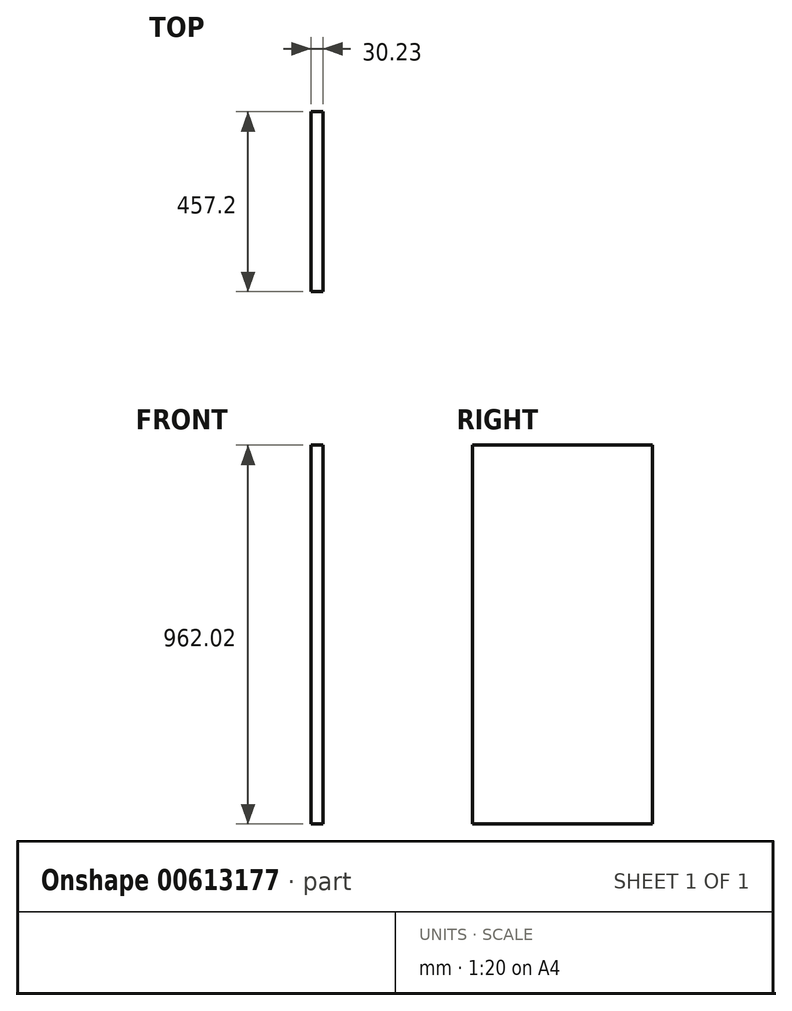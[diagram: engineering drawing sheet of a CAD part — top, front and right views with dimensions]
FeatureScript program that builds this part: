
annotation { "Feature Type Name" : "Feature", "Feature Type Description" : "" }
export const myFeature = defineFeature(function(context is Context, id is Id, definition is map)
    precondition{}
    {
        {
            var Q0;
            Q0=qCreatedBy(makeId("Right.planeOp"),FACE);
            var sketch = newSketch(context, id + "F0", { "sketchPlane" : qUnion([Q0])});
            skLineSegment(sketch, "E0.bottom", {"start": v(228.6, 481.01) * mm, "end": v(-228.6, 481.01) * mm});
            skLineSegment(sketch, "E0.top", {"start": v(228.6, -481.01) * mm, "end": v(-228.6, -481.01) * mm});
            skLineSegment(sketch, "E0.left", {"start": v(228.6, 481.01) * mm, "end": v(228.6, -481.01) * mm});
            skLineSegment(sketch, "E0.right", {"start": v(-228.6, 481.01) * mm, "end": v(-228.6, -481.01) * mm});
            skPoint(sketch, "E0.middle", {"position": v(0, 0) * mm});
            skSolve(sketch);
        }
        {
            var Q0;
            Q0=makeQuery(id+"F0.imprint","IMPRINT",FACE,{"disambiguationData":[TD([[makeQuery(id+"F0.imprint","IMPRINT",EDGE,{"derivedFrom":sQuery(id+"F0.wireOp",EDGE,"E0.bottom")}),1.0]])]});
            extrude(context, id + "F1", {"entities" : qUnion([Q0]), "depth" : 30.23 * mm, "offsetDistance" : 25.4 * mm});
        }
    });
